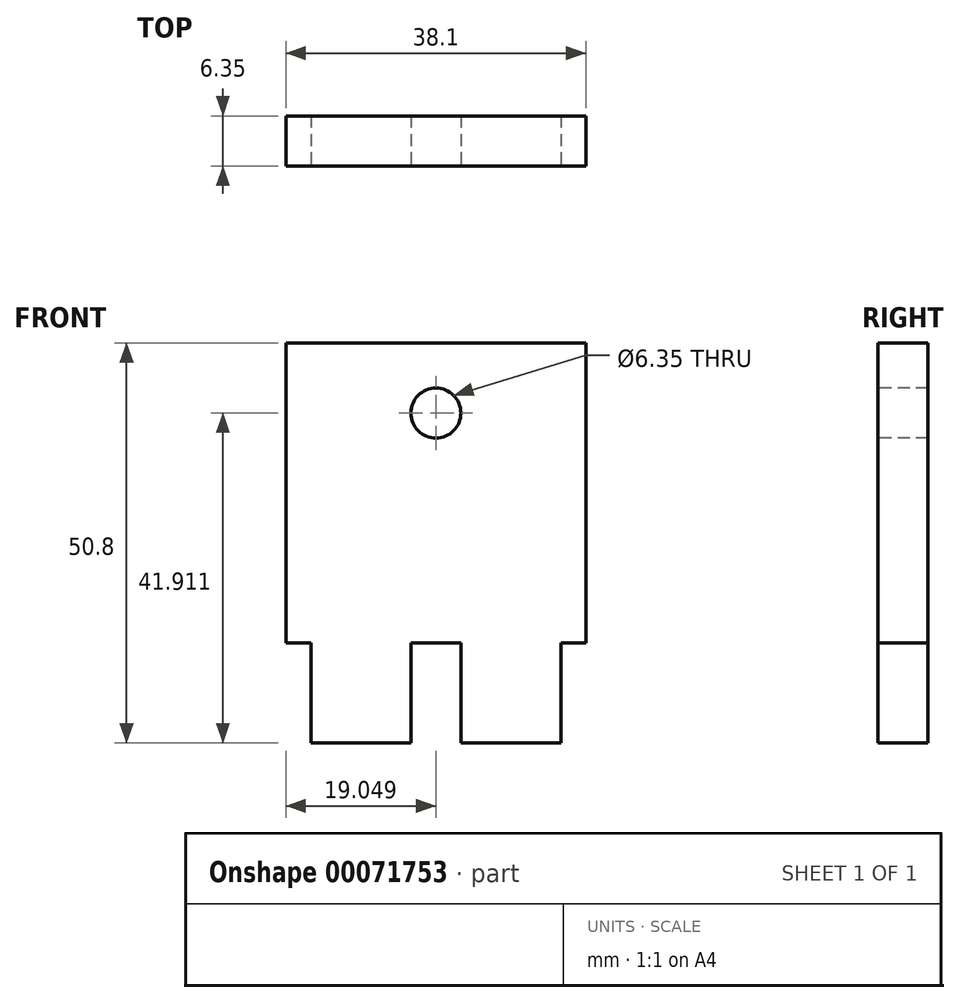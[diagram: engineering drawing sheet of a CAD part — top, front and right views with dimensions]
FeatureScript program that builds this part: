
annotation { "Feature Type Name" : "Feature", "Feature Type Description" : "" }
export const myFeature = defineFeature(function(context is Context, id is Id, definition is map)
    precondition{}
    {
        {
            var Q0;
            Q0=qCreatedBy(makeId("Front.planeOp"),FACE);
            var sketch = newSketch(context, id + "F0", { "sketchPlane" : qUnion([Q0])});
            skLineSegment(sketch, "E0.bottom", {"start": v(-14.46, 32.53) * mm, "end": v(23.64, 32.53) * mm});
            skLineSegment(sketch, "E0.top", {"start": v(-14.46, -18.27) * mm, "end": v(23.64, -18.27) * mm});
            skLineSegment(sketch, "E0.left", {"start": v(-14.46, 32.53) * mm, "end": v(-14.46, -18.27) * mm});
            skLineSegment(sketch, "E0.right", {"start": v(23.64, 32.53) * mm, "end": v(23.64, -18.27) * mm});
            skSolve(sketch);
        }
        {
            var Q0;
            Q0 = qSketchRegion(id + "F0", true);
            extrude(context, id + "F1", {"entities" : qUnion([Q0]), "depth" : 6.35 * mm});
        }
        {
            var Q0;
            Q0=makeQuery(id+"F1.opExtrude","CAP_FACE",FACE,{"disambiguationData":[OSD([sQuery(id+"F0.wireOp",EDGE,"E0.bottom"),sQuery(id+"F0.wireOp",EDGE,"E0.top"),sQuery(id+"F0.wireOp",EDGE,"E0.left"),sQuery(id+"F0.wireOp",EDGE,"E0.right")])],"isStart":false});
            var sketch = newSketch(context, id + "F2", { "sketchPlane" : qUnion([Q0])});
            skLineSegment(sketch, "E1", {"start": v(4.59, 32.53) * mm, "end": v(4.59, -18.27) * mm, "construction": true});
            skLineSegment(sketch, "E2", {"start": v(-14.46, 23.64) * mm, "end": v(23.64, 23.64) * mm, "construction": true});
            skCircle(sketch, "E3", {"center": v(4.59, 23.64) * mm, "radius": 3.18 * mm});
            skSolve(sketch);
        }
        {
            var Q0;
            Q0=makeQuery(id+"F2.imprint","IMPRINT",FACE,{"disambiguationData":[TD([[makeQuery(id+"F2.imprint","IMPRINT",EDGE,{"derivedFrom":sQuery(id+"F2.wireOp",EDGE,"E3")}),1.0]])]});
            extrude(context, id + "F3", {"entities" : qUnion([Q0]), "operationType" : NewBodyOperationType.REMOVE, "endBound" : BoundingType.THROUGH_ALL, "oppositeDirection" : true, "depth" : 25.4 * mm});
        }
        {
            var Q0;
            Q0=makeQuery(id+"F1.opExtrude","CAP_FACE",FACE,{"disambiguationData":[OSD([sQuery(id+"F0.wireOp",EDGE,"E0.bottom"),sQuery(id+"F0.wireOp",EDGE,"E0.top"),sQuery(id+"F0.wireOp",EDGE,"E0.left"),sQuery(id+"F0.wireOp",EDGE,"E0.right")])],"isStart":false});
            var sketch = newSketch(context, id + "F4", { "sketchPlane" : qUnion([Q0])});
            skLineSegment(sketch, "E4.bottom", {"start": v(-14.46, -5.57) * mm, "end": v(-11.29, -5.57) * mm});
            skLineSegment(sketch, "E4.top", {"start": v(-14.46, -18.27) * mm, "end": v(-11.29, -18.27) * mm});
            skLineSegment(sketch, "E4.left", {"start": v(-14.46, -5.57) * mm, "end": v(-14.46, -18.27) * mm});
            skLineSegment(sketch, "E4.right", {"start": v(-11.29, -5.57) * mm, "end": v(-11.29, -18.27) * mm});
            skLineSegment(sketch, "E5.bottom", {"start": v(23.64, -5.57) * mm, "end": v(20.46, -5.57) * mm});
            skLineSegment(sketch, "E5.top", {"start": v(23.64, -18.27) * mm, "end": v(20.46, -18.27) * mm});
            skLineSegment(sketch, "E5.left", {"start": v(23.64, -5.57) * mm, "end": v(23.64, -18.27) * mm});
            skLineSegment(sketch, "E5.right", {"start": v(20.46, -5.57) * mm, "end": v(20.46, -18.27) * mm});
            skSolve(sketch);
        }
        {
            var Q0;
            Q0 = qSketchRegion(id + "F4", true);
            extrude(context, id + "F5", {"entities" : qUnion([Q0]), "operationType" : NewBodyOperationType.REMOVE, "endBound" : BoundingType.THROUGH_ALL, "oppositeDirection" : true, "depth" : 25.4 * mm});
        }
        {
            var Q0;
            Q0=makeQuery(id+"F1.opExtrude","CAP_FACE",FACE,{"disambiguationData":[OSD([sQuery(id+"F0.wireOp",EDGE,"E0.bottom"),sQuery(id+"F0.wireOp",EDGE,"E0.top"),sQuery(id+"F0.wireOp",EDGE,"E0.left"),sQuery(id+"F0.wireOp",EDGE,"E0.right")])],"isStart":false});
            var sketch = newSketch(context, id + "F6", { "sketchPlane" : qUnion([Q0])});
            skLineSegment(sketch, "E6", {"start": v(4.59, 32.53) * mm, "end": v(4.59, -18.27) * mm, "construction": true});
            skLineSegment(sketch, "E7.bottom", {"start": v(1.41, -5.57) * mm, "end": v(7.76, -5.57) * mm});
            skLineSegment(sketch, "E7.top", {"start": v(1.41, -18.27) * mm, "end": v(7.76, -18.27) * mm});
            skLineSegment(sketch, "E7.left", {"start": v(1.41, -5.57) * mm, "end": v(1.41, -18.27) * mm});
            skLineSegment(sketch, "E7.right", {"start": v(7.76, -5.57) * mm, "end": v(7.76, -18.27) * mm});
            skSolve(sketch);
        }
        {
            var Q0;
            Q0 = qSketchRegion(id + "F6", true);
            extrude(context, id + "F7", {"entities" : qUnion([Q0]), "operationType" : NewBodyOperationType.REMOVE, "oppositeDirection" : true, "depth" : 25.4 * mm});
        }
    });
